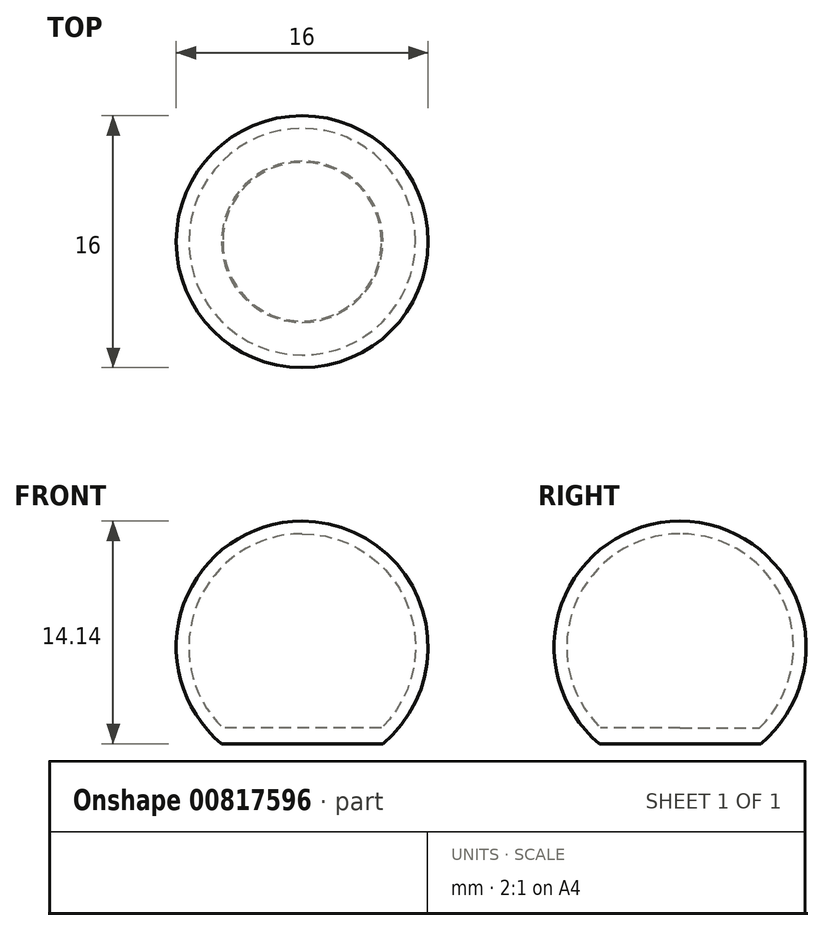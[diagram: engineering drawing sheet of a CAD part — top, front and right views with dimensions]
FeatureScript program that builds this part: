
annotation { "Feature Type Name" : "Feature", "Feature Type Description" : "" }
export const myFeature = defineFeature(function(context is Context, id is Id, definition is map)
    precondition{}
    {
        {
            var Q0;
            Q0=qCreatedBy(makeId("Front.planeOp"),FACE);
            var sketch = newSketch(context, id + "F0", { "sketchPlane" : qUnion([Q0])});
            skArc(sketch, "E0", {"start": v(0, -8) * mm, "mid": v(8, 0) * mm, "end": v(0, 8) * mm});
            skLineSegment(sketch, "E1", {"start": v(0, 0) * mm, "end": v(0, 8) * mm});
            skLineSegment(sketch, "E2", {"start": v(0, 0) * mm, "end": v(0, -8) * mm});
            skLineSegment(sketch, "E3", {"start": v(0, -8) * mm, "end": v(0, -8) * mm});
            skArc(sketch, "E4", {"start": v(0, -7.2) * mm, "mid": v(7.2, 0) * mm, "end": v(0, 7.2) * mm});
            skLineSegment(sketch, "E5", {"start": v(0, -5.14) * mm, "end": v(6.13, -5.14) * mm});
            skLineSegment(sketch, "E6", {"start": v(6.13, -5.14) * mm, "end": v(8.46, -2.36) * mm, "construction": true});
            skLineSegment(sketch, "E7", {"start": v(0, -6.14) * mm, "end": v(5.13, -6.14) * mm});
            skSolve(sketch);
        }
        {
            var Q0;
            {var subQ0=sQuery(id+"F0.wireOp",EDGE,"E1");var subQ1=sQuery(id+"F0.wireOp",EDGE,"E0");var subQ2=makeQuery(id+"F0.imprint","INTERSECT",VERTEX,{"derivedFrom":[subQ1,subQ0]});Q0=makeQuery(id+"F0.imprint","IMPRINT",FACE,{"disambiguationData":[TD([[makeQuery(id+"F0.imprint","IMPRINT",EDGE,{"disambiguationData":[TD([[subQ2,1.0]])],"derivedFrom":subQ1}),1.0]])]});}
            var Q1;
            {var subQ0=sQuery(id+"F0.wireOp",EDGE,"E1");var subQ1=sQuery(id+"F0.wireOp",EDGE,"E0");var subQ2=makeQuery(id+"F0.imprint","INTERSECT",VERTEX,{"derivedFrom":[subQ1,subQ0]});Q1=makeQuery(id+"F0.imprint","IMPRINT",FACE,{"disambiguationData":[TD([[makeQuery(id+"F0.imprint","IMPRINT",EDGE,{"disambiguationData":[TD([[subQ2,1.0]])],"derivedFrom":subQ1}),1.0]])]});}
            var Q2;
            {var subQ0=sQuery(id+"F0.wireOp",EDGE,"E5");var subQ1=sQuery(id+"F0.wireOp",EDGE,"E0");var subQ2=makeQuery(id+"F0.imprint","INTERSECT",VERTEX,{"derivedFrom":[subQ1,subQ0]});Q2=makeQuery(id+"F0.imprint","IMPRINT",FACE,{"disambiguationData":[TD([[makeQuery(id+"F0.imprint","IMPRINT",EDGE,{"disambiguationData":[TD([[subQ2,1.0]])],"derivedFrom":subQ1}),1.0]])]});}
            var Q3;
            {var subQ0=sQuery(id+"F0.wireOp",EDGE,"E5");var subQ1=sQuery(id+"F0.wireOp",EDGE,"E2");var subQ2=makeQuery(id+"F0.imprint","INTERSECT",VERTEX,{"derivedFrom":[subQ1,subQ0]});Q3=makeQuery(id+"F0.imprint","IMPRINT",FACE,{"disambiguationData":[TD([[makeQuery(id+"F0.imprint","IMPRINT",EDGE,{"disambiguationData":[TD([[subQ2,-1.0]])],"derivedFrom":subQ1}),1.0]])]});}
            var Q4;
            Q4=sQuery(id+"F0.wireOp",EDGE,"E1");
            revolve(context, id + "F1", {"surfaceOperationType" : NewSurfaceOperationType.NEW, "entities" : qUnion([Q0, Q1, Q2, Q3]), "axis" : qUnion([Q4]), "revolveType" : RevolveType.FULL});
        }
    });
